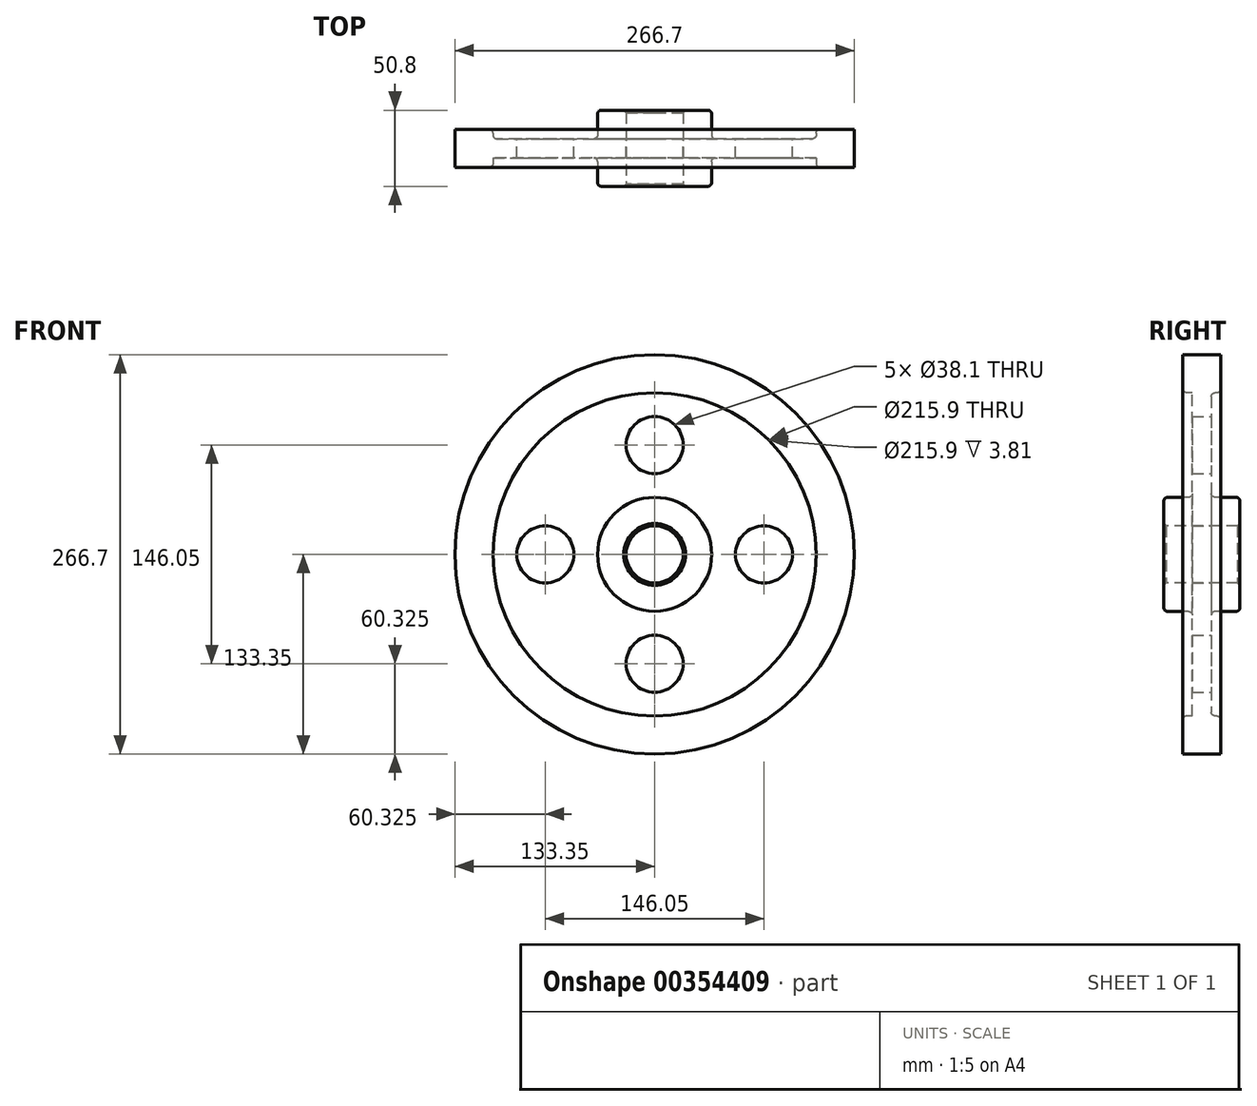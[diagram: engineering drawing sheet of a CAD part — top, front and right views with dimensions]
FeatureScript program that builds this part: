
annotation { "Feature Type Name" : "Feature", "Feature Type Description" : "" }
export const myFeature = defineFeature(function(context is Context, id is Id, definition is map)
    precondition{}
    {
        {
            var Q0;
            Q0=qCreatedBy(makeId("Right.planeOp"),FACE);
            var sketch = newSketch(context, id + "F0", { "sketchPlane" : qUnion([Q0])});
            skLineSegment(sketch, "E0", {"start": v(0, 0) * mm, "end": v(93.85, 0) * mm, "construction": true});
            skLineSegment(sketch, "E1.0", {"start": v(0, 19.05) * mm, "end": v(25.4, 19.05) * mm});
            skLineSegment(sketch, "E2.0", {"start": v(6.35, 38.1) * mm, "end": v(25.4, 38.1) * mm});
            skLineSegment(sketch, "E3.0", {"start": v(6.35, 107.95) * mm, "end": v(12.7, 107.95) * mm});
            skLineSegment(sketch, "E4.0", {"start": v(0, 133.35) * mm, "end": v(12.7, 133.35) * mm});
            skLineSegment(sketch, "E5", {"start": v(0, 133.35) * mm, "end": v(0, 0) * mm, "construction": true});
            skLineSegment(sketch, "E6.0", {"start": v(6.35, 107.95) * mm, "end": v(6.35, 38.1) * mm});
            skLineSegment(sketch, "E7.0", {"start": v(12.7, 133.35) * mm, "end": v(12.7, 107.95) * mm});
            skLineSegment(sketch, "E8.trimOffspring", {"start": v(25.4, 38.1) * mm, "end": v(25.4, 19.05) * mm});
            skLineSegment(sketch, "E9.MirrorCS", {"start": v(0, 133.35) * mm, "end": v(-12.7, 133.35) * mm});
            skLineSegment(sketch, "E10.MirrorCS", {"start": v(-12.7, 133.35) * mm, "end": v(-12.7, 107.95) * mm});
            skLineSegment(sketch, "E11.MirrorCS", {"start": v(-6.35, 107.95) * mm, "end": v(-6.35, 38.1) * mm});
            skLineSegment(sketch, "E12.MirrorCS", {"start": v(-25.4, 38.1) * mm, "end": v(-25.4, 19.05) * mm});
            skLineSegment(sketch, "E13.MirrorCS", {"start": v(0, 19.05) * mm, "end": v(-25.4, 19.05) * mm});
            skLineSegment(sketch, "E14.MirrorCS", {"start": v(-6.35, 38.1) * mm, "end": v(-25.4, 38.1) * mm});
            skLineSegment(sketch, "E15.MirrorCS", {"start": v(-6.35, 107.95) * mm, "end": v(-12.7, 107.95) * mm});
            skSolve(sketch);
        }
        {
            var Q0;
            Q0=makeQuery(id+"F0.imprint","IMPRINT",FACE,{"disambiguationData":[TD([[makeQuery(id+"F0.imprint","IMPRINT",EDGE,{"derivedFrom":sQuery(id+"F0.wireOp",EDGE,"E1.0")}),1.0]])]});
            var Q1;
            Q1=sQuery(id+"F0.wireOp",EDGE,"E0");
            revolve(context, id + "F1", {"entities" : qUnion([Q0]), "axis" : qUnion([Q1]), "revolveType" : RevolveType.FULL});
        }
        {
            var Q0;
            Q0=makeQuery(id+"F1.opRevolve","SWEPT_FACE",FACE,{"disambiguationData":[OSD([sQuery(id+"F0.wireOp",EDGE,"E6.0")])]});
            var sketch = newSketch(context, id + "F2", { "sketchPlane" : qUnion([Q0])});
            skLineSegment(sketch, "E16", {"start": v(0, 0) * mm, "end": v(0, 73.03) * mm});
            skCircle(sketch, "E17", {"center": v(0, 73.03) * mm, "radius": 19.05 * mm});
            skCircle(sketch, "E18.1.0", {"center": v(-73.03, 0) * mm, "radius": 19.05 * mm});
            skCircle(sketch, "E18.2.0", {"center": v(0, -73.03) * mm, "radius": 19.05 * mm});
            skCircle(sketch, "E18.3.0", {"center": v(73.03, 0) * mm, "radius": 19.05 * mm});
            skPoint(sketch, "E18.center", {"position": v(0, 0) * mm});
            skSolve(sketch);
        }
        {
            var Q0;
            Q0=makeQuery(id+"F2.imprint","IMPRINT",FACE,{"disambiguationData":[TD([[makeQuery(id+"F2.imprint","IMPRINT",EDGE,{"derivedFrom":sQuery(id+"F2.wireOp",EDGE,"E18.2.0")}),1.0]])]});
            var Q1;
            Q1=makeQuery(id+"F2.imprint","IMPRINT",FACE,{"disambiguationData":[TD([[makeQuery(id+"F2.imprint","IMPRINT",EDGE,{"derivedFrom":sQuery(id+"F2.wireOp",EDGE,"E18.3.0")}),1.0]])]});
            var Q2;
            Q2=makeQuery(id+"F2.imprint","IMPRINT",FACE,{"disambiguationData":[TD([[makeQuery(id+"F2.imprint","IMPRINT",EDGE,{"derivedFrom":sQuery(id+"F2.wireOp",EDGE,"E17")}),1.0]])]});
            var Q3;
            Q3=makeQuery(id+"F2.imprint","IMPRINT",FACE,{"disambiguationData":[TD([[makeQuery(id+"F2.imprint","IMPRINT",EDGE,{"derivedFrom":sQuery(id+"F2.wireOp",EDGE,"E18.1.0")}),1.0]])]});
            extrude(context, id + "F3", {"entities" : qUnion([Q0, Q1, Q2, Q3]), "operationType" : NewBodyOperationType.REMOVE, "oppositeDirection" : true, "depth" : 25.4 * mm});
        }
        {
            var Q0;
            Q0=makeQuery(id+"F1.opRevolve","SWEPT_EDGE",EDGE,{"disambiguationData":[OSD([sQuery(id+"F0.wireOp",EDGE,"E2.0"),sQuery(id+"F0.wireOp",EDGE,"E6.0")])]});
            var Q1;
            Q1=makeQuery(id+"F1.opRevolve","SWEPT_EDGE",EDGE,{"disambiguationData":[OSD([sQuery(id+"F0.wireOp",EDGE,"E2.0"),sQuery(id+"F0.wireOp",EDGE,"E8.trimOffspring")])]});
            var Q2;
            Q2=makeQuery(id+"F1.opRevolve","SWEPT_EDGE",EDGE,{"disambiguationData":[OSD([sQuery(id+"F0.wireOp",EDGE,"E3.0"),sQuery(id+"F0.wireOp",EDGE,"E6.0")])]});
            var Q3;
            Q3=makeQuery(id+"F1.opRevolve","SWEPT_EDGE",EDGE,{"disambiguationData":[OSD([sQuery(id+"F0.wireOp",EDGE,"E3.0"),sQuery(id+"F0.wireOp",EDGE,"E7.0")])]});
            var Q4;
            Q4=makeQuery(id+"F1.opRevolve","SWEPT_EDGE",EDGE,{"disambiguationData":[OSD([sQuery(id+"F0.wireOp",EDGE,"E11.MirrorCS"),sQuery(id+"F0.wireOp",EDGE,"E14.MirrorCS")])]});
            var Q5;
            Q5=makeQuery(id+"F1.opRevolve","SWEPT_EDGE",EDGE,{"disambiguationData":[OSD([sQuery(id+"F0.wireOp",EDGE,"E12.MirrorCS"),sQuery(id+"F0.wireOp",EDGE,"E14.MirrorCS")])]});
            var Q6;
            Q6=makeQuery(id+"F1.opRevolve","SWEPT_EDGE",EDGE,{"disambiguationData":[OSD([sQuery(id+"F0.wireOp",EDGE,"E10.MirrorCS"),sQuery(id+"F0.wireOp",EDGE,"E15.MirrorCS")])]});
            fillet(context, id + "F4", {"entities" : qUnion([Q0, Q1, Q2, Q3, Q4, Q5, Q6]), "radius" : 2.54 * mm, "tangentPropagation" : true, "allowEdgeOverflow" : false});
        }
        {
            var Q0;
            Q0=makeQuery(id+"F1.opRevolve","SWEPT_EDGE",EDGE,{"disambiguationData":[OSD([sQuery(id+"F0.wireOp",EDGE,"E1.0"),sQuery(id+"F0.wireOp",EDGE,"E8.trimOffspring")])]});
            var Q1;
            Q1=makeQuery(id+"F1.opRevolve","SWEPT_EDGE",EDGE,{"disambiguationData":[OSD([sQuery(id+"F0.wireOp",EDGE,"E12.MirrorCS"),sQuery(id+"F0.wireOp",EDGE,"E13.MirrorCS")])]});
            chamfer(context, id + "F5", {"entities" : qUnion([Q0, Q1]), "width" : 1.59 * mm, "tangentPropagation" : true});
        }
    });
